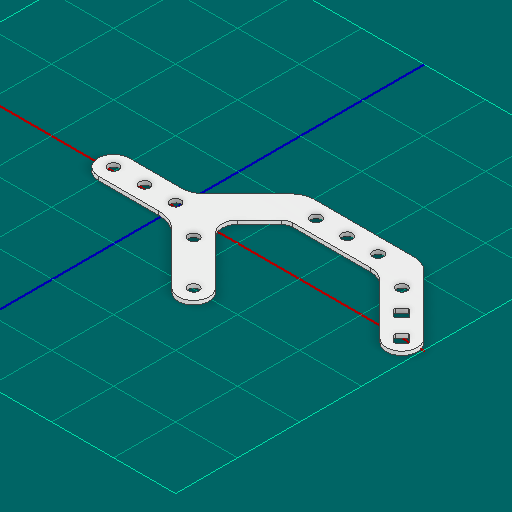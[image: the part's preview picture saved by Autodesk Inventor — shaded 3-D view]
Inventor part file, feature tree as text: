
AUTODESK INVENTOR PART (.ipt)
format: ipt  version: 2025 (Build 290162000, 162)  size: 209,408 bytes
history: native  units: in
note: dims shown in document units (in); Inventor stores cm internally (conversion verified against a paired STEP export)
features: other x5, sketch x1
ambient origin geometry x8: Origin, YZ Plane, XZ Plane, XY Plane, X Axis, Y Axis, Z Axis, Center Point
bodies: Solid1 (feature_tree)
feature tree (6):
  other  "join_gusset.ipt"
  other  "Blocks"
  other  "main"
  other  "Solid1::join_gusset.ipt"
  other  "TaggingFeature1"
  sketch  "Sketch1"  dims[d0=0.3937in d5=0.5in d6=135.0deg d7=0.375in d8=0.5in d9=0.375in d10=0.375in d11=0.5in d12=0.1875in d15=1.25in d16=0.5in d17=45.0deg d18=0.25in d19=0.172in d20=0.25in d22=0.172in d23=0.5in d24=0.172in d25=0.5in]
